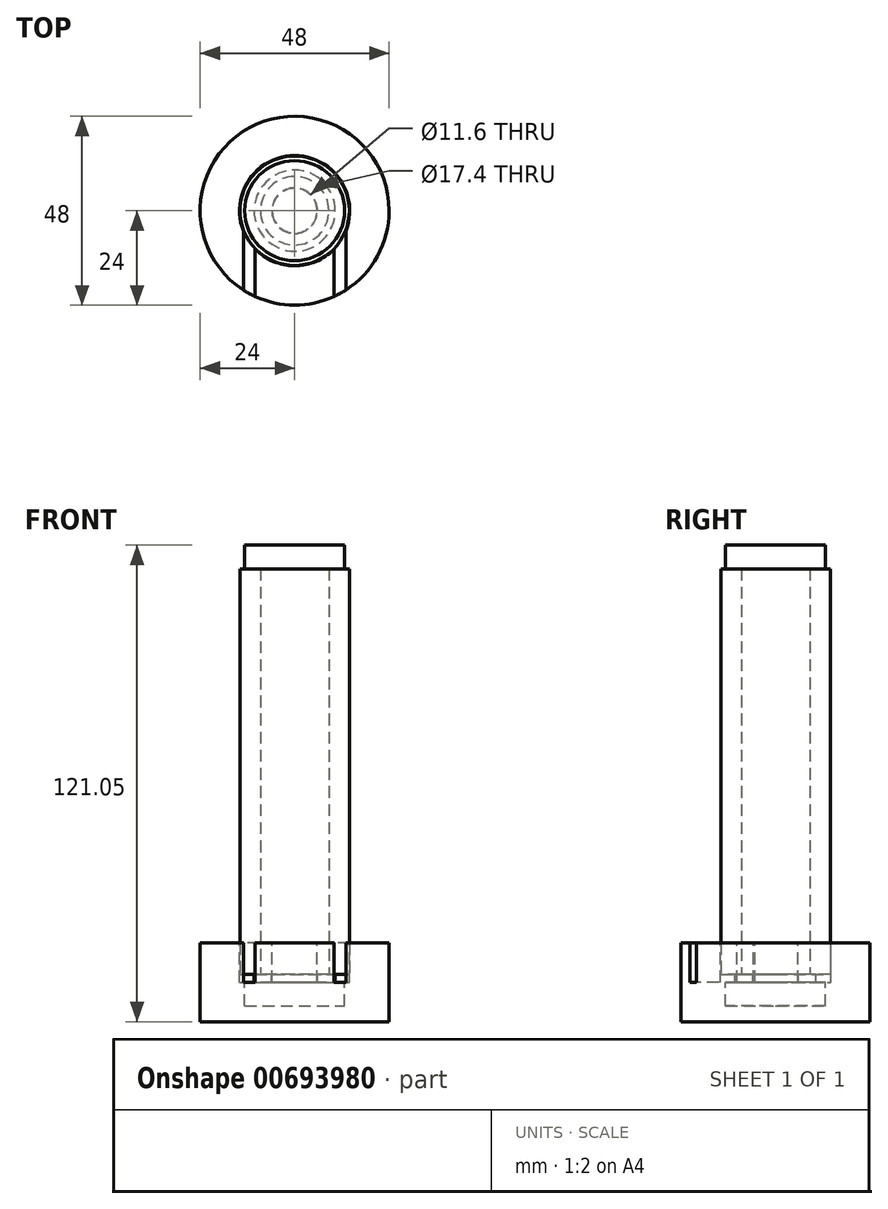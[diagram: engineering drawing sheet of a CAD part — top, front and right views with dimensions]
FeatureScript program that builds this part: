
annotation { "Feature Type Name" : "Feature", "Feature Type Description" : "" }
export const myFeature = defineFeature(function(context is Context, id is Id, definition is map)
    precondition{}
    {
        {
            var Q0;
            Q0=qCreatedBy(makeId("Top.planeOp"),FACE);
            var sketch = newSketch(context, id + "F0", { "sketchPlane" : qUnion([Q0])});
            skCircle(sketch, "E0", {"center": v(0, 0) * mm, "radius": 13.9 * mm});
            skCircle(sketch, "E1", {"center": v(0, 0) * mm, "radius": 8.7 * mm});
            skSolve(sketch);
        }
        {
            var Q0;
            Q0 = qSketchRegion(id + "F0", true);
            extrude(context, id + "F1", {"entities" : qUnion([Q0]), "endBound" : BoundingType.SYMMETRIC, "depth" : 103 * mm, "offsetDistance" : 25 * mm});
        }
        {
            var Q0;
            Q0=makeQuery(id+"F1.opExtrude","CAP_FACE",FACE,{"disambiguationData":[OSD([sQuery(id+"F0.wireOp",EDGE,"E0"),sQuery(id+"F0.wireOp",EDGE,"E1")])],"isStart":false});
            var sketch = newSketch(context, id + "F2", { "sketchPlane" : qUnion([Q0])});
            skCircle(sketch, "E2", {"center": v(0, 0) * mm, "radius": 12.7 * mm});
            skSolve(sketch);
        }
        {
            var Q0;
            Q0 = qSketchRegion(id + "F2", true);
            extrude(context, id + "F3", {"entities" : qUnion([Q0]), "depth" : 6 * mm, "offsetDistance" : 25 * mm});
        }
        {
            var Q0;
            Q0=makeQuery(id+"F1.opExtrude","CAP_FACE",FACE,{"disambiguationData":[OSD([sQuery(id+"F0.wireOp",EDGE,"E0"),sQuery(id+"F0.wireOp",EDGE,"E1")])],"isStart":true});
            var sketch = newSketch(context, id + "F4", { "sketchPlane" : qUnion([Q0])});
            skCircle(sketch, "E3", {"center": v(0, 0) * mm, "radius": 10.3 * mm});
            skCircle(sketch, "E4", {"center": v(0, 0) * mm, "radius": 5.8 * mm});
            skSolve(sketch);
        }
        {
            var Q0;
            Q0 = qSketchRegion(id + "F4", true);
            extrude(context, id + "F5", {"entities" : qUnion([Q0]), "depth" : 2.05 * mm, "offsetDistance" : 25 * mm});
        }
        {
            var Q0;
            Q0=makeQuery(id+"F5.opExtrude","CAP_FACE",FACE,{"disambiguationData":[OSD([sQuery(id+"F4.wireOp",EDGE,"E3"),sQuery(id+"F4.wireOp",EDGE,"E4")])],"isStart":false});
            var sketch = newSketch(context, id + "F6", { "sketchPlane" : qUnion([Q0])});
            skCircle(sketch, "E5", {"center": v(0, 0) * mm, "radius": 12.7 * mm});
            skSolve(sketch);
        }
        {
            var Q0;
            Q0 = qSketchRegion(id + "F6", true);
            extrude(context, id + "F7", {"entities" : qUnion([Q0]), "depth" : 6 * mm, "offsetDistance" : 25 * mm});
        }
        {
            var Q0;
            Q0=qCreatedBy(makeId("Front.planeOp"),FACE);
            var sketch = newSketch(context, id + "F8", { "sketchPlane" : qUnion([Q0])});
            skLineSegment(sketch, "E6", {"start": v(12.7, 57.5) * mm, "end": v(12.7, 51.5) * mm, "construction": true});
            skLineSegment(sketch, "E7", {"start": v(-12.7, 51.5) * mm, "end": v(-12.7, 57.5) * mm, "construction": true});
            skLineSegment(sketch, "E8", {"start": v(13.9, 51.5) * mm, "end": v(13.9, -51.5) * mm, "construction": true});
            skLineSegment(sketch, "E9", {"start": v(-13.9, -51.5) * mm, "end": v(-13.9, 51.5) * mm, "construction": true});
            skLineSegment(sketch, "E10", {"start": v(-10.3, -53.55) * mm, "end": v(-10.3, -51.5) * mm, "construction": true});
            skLineSegment(sketch, "E11", {"start": v(10.3, -51.5) * mm, "end": v(10.3, -53.55) * mm, "construction": true});
            skLineSegment(sketch, "E12", {"start": v(-12.7, -59.55) * mm, "end": v(-12.7, -53.55) * mm, "construction": true});
            skLineSegment(sketch, "E13", {"start": v(12.7, -53.55) * mm, "end": v(12.7, -59.55) * mm, "construction": true});
            skLineSegment(sketch, "E14", {"start": v(-5.8, -53.55) * mm, "end": v(-5.8, -51.5) * mm, "construction": true});
            skLineSegment(sketch, "E15", {"start": v(5.8, -51.5) * mm, "end": v(5.8, -53.55) * mm, "construction": true});
            skLineSegment(sketch, "E16", {"start": v(-12.7, 57.5) * mm, "end": v(12.7, 57.5) * mm, "construction": true});
            skLineSegment(sketch, "E17", {"start": v(12.7, 51.5) * mm, "end": v(13.9, 51.5) * mm, "construction": true});
            skLineSegment(sketch, "E18", {"start": v(-12.7, 51.5) * mm, "end": v(-13.9, 51.5) * mm, "construction": true});
            skLineSegment(sketch, "E19", {"start": v(-13.9, -51.5) * mm, "end": v(-10.3, -51.5) * mm, "construction": true});
            skLineSegment(sketch, "E20", {"start": v(-10.3, -53.55) * mm, "end": v(-12.7, -53.55) * mm, "construction": true});
            skLineSegment(sketch, "E21", {"start": v(10.3, -53.55) * mm, "end": v(12.7, -53.55) * mm, "construction": true});
            skLineSegment(sketch, "E22", {"start": v(13.9, -51.5) * mm, "end": v(10.3, -51.5) * mm, "construction": true});
            skLineSegment(sketch, "E23", {"start": v(5.8, -51.5) * mm, "end": v(10.3, -51.5) * mm, "construction": true});
            skLineSegment(sketch, "E24", {"start": v(10.3, -53.55) * mm, "end": v(5.8, -53.55) * mm, "construction": true});
            skLineSegment(sketch, "E25", {"start": v(-5.8, -53.55) * mm, "end": v(-10.3, -53.55) * mm, "construction": true});
            skLineSegment(sketch, "E26", {"start": v(-10.3, -51.5) * mm, "end": v(-5.8, -51.5) * mm, "construction": true});
            skLineSegment(sketch, "E27", {"start": v(-12.7, -59.55) * mm, "end": v(12.7, -59.55) * mm, "construction": true});
            skLineSegment(sketch, "E28", {"start": v(-5.8, -53.55) * mm, "end": v(5.8, -53.55) * mm, "construction": true});
            skLineSegment(sketch, "E29", {"start": v(-12.7, 51.5) * mm, "end": v(12.7, 51.5) * mm, "construction": true});
            skLineSegment(sketch, "E30", {"start": v(5.7, -43.55) * mm, "end": v(5.7, -53.55) * mm});
            skLineSegment(sketch, "E31", {"start": v(5.7, -53.55) * mm, "end": v(14, -53.55) * mm});
            skLineSegment(sketch, "E32", {"start": v(8.7, 51.5) * mm, "end": v(8.7, -51.5) * mm, "construction": true});
            skLineSegment(sketch, "E33", {"start": v(-8.7, -51.5) * mm, "end": v(-8.7, 51.5) * mm, "construction": true});
            skLineSegment(sketch, "E34", {"start": v(14, -53.55) * mm, "end": v(14, -43.55) * mm});
            skLineSegment(sketch, "E35", {"start": v(14, -43.55) * mm, "end": v(24, -43.55) * mm});
            skLineSegment(sketch, "E36", {"start": v(24, -43.55) * mm, "end": v(24, -63.55) * mm});
            skLineSegment(sketch, "E37", {"start": v(24, -63.55) * mm, "end": v(0, -63.55) * mm});
            skLineSegment(sketch, "E38", {"start": v(0, -63.55) * mm, "end": v(0, -43.55) * mm});
            skLineSegment(sketch, "E39", {"start": v(0, -43.55) * mm, "end": v(5.7, -43.55) * mm});
            skLineSegment(sketch, "E40", {"start": v(0, 10.57) * mm, "end": v(0, -10.73) * mm, "construction": true});
            skSolve(sketch);
        }
        {
            var Q0;
            Q0 = qSketchRegion(id + "F8", true);
            var Q1;
            Q1=sQuery(id+"F8.wireOp",EDGE,"E40");
            revolve(context, id + "F9", {"surfaceOperationType" : NewSurfaceOperationType.NEW, "entities" : qUnion([Q0]), "axis" : qUnion([Q1]), "revolveType" : RevolveType.FULL});
        }
        {
            var Q0;
            Q0=makeQuery(id+"F9.opRevolve","SWEPT_FACE",FACE,{"disambiguationData":[OSD([sQuery(id+"F8.wireOp",EDGE,"E31")])]});
            var sketch = newSketch(context, id + "F10", { "sketchPlane" : qUnion([Q0])});
            skLineSegment(sketch, "E41.bottom", {"start": v(-13, 0) * mm, "end": v(-10, 0) * mm});
            skLineSegment(sketch, "E41.top", {"start": v(-13, -25) * mm, "end": v(-10, -25) * mm});
            skLineSegment(sketch, "E41.left", {"start": v(-13, 0) * mm, "end": v(-13, -25) * mm});
            skLineSegment(sketch, "E41.right", {"start": v(-10, 0) * mm, "end": v(-10, -25) * mm});
            skLineSegment(sketch, "E42.bottom", {"start": v(10, 0) * mm, "end": v(13, 0) * mm});
            skLineSegment(sketch, "E42.top", {"start": v(10, -25) * mm, "end": v(13, -25) * mm});
            skLineSegment(sketch, "E42.left", {"start": v(10, 0) * mm, "end": v(10, -25) * mm});
            skLineSegment(sketch, "E42.right", {"start": v(13, 0) * mm, "end": v(13, -25) * mm});
            skLineSegment(sketch, "E43", {"start": v(0, 5.61) * mm, "end": v(0, -6.07) * mm, "construction": true});
            skLineSegment(sketch, "E44", {"start": v(-3.9, 0) * mm, "end": v(3.32, 0) * mm, "construction": true});
            skSolve(sketch);
        }
        {
            var Q0;
            Q0 = qSketchRegion(id + "F10", true);
            extrude(context, id + "F11", {"entities" : qUnion([Q0]), "operationType" : NewBodyOperationType.REMOVE, "endBound" : BoundingType.UP_TO_NEXT, "depth" : 25 * mm, "offsetDistance" : 25 * mm});
        }
    });
